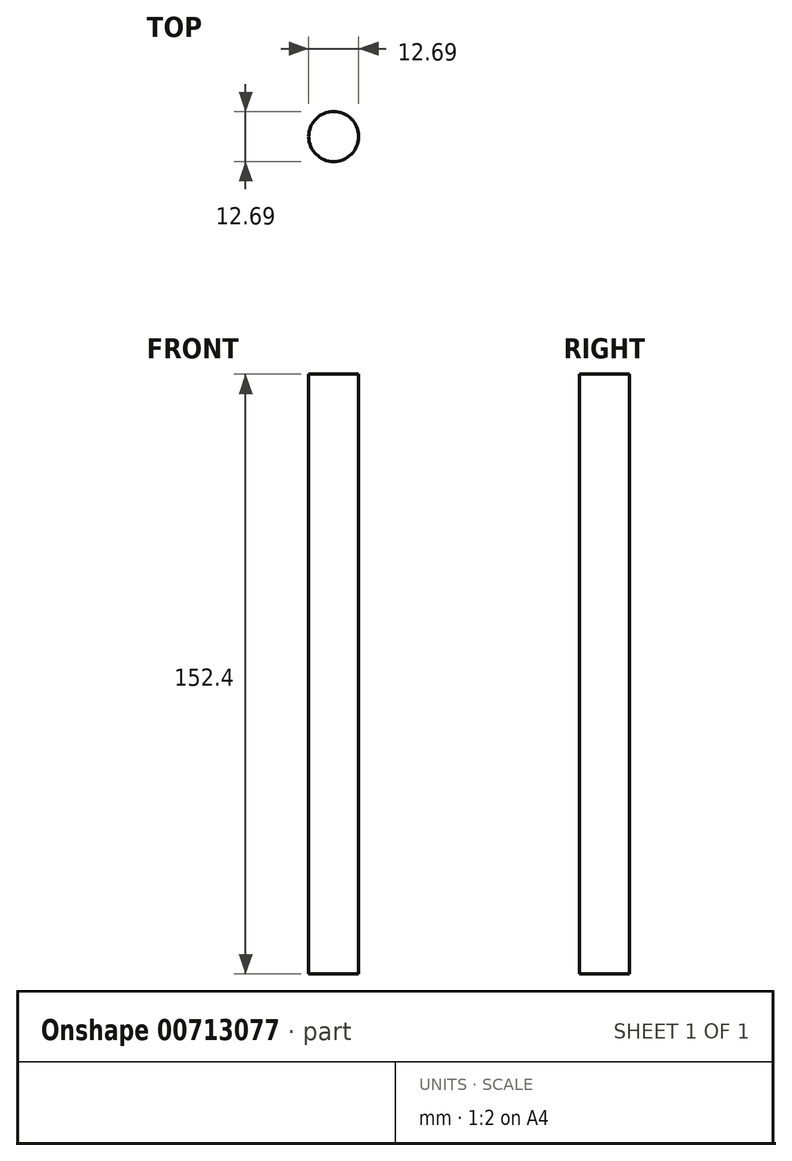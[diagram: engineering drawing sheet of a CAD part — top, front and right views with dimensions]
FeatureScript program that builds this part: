
annotation { "Feature Type Name" : "Feature", "Feature Type Description" : "" }
export const myFeature = defineFeature(function(context is Context, id is Id, definition is map)
    precondition{}
    {
        {
            var Q0;
            Q0=qCreatedBy(makeId("Top.planeOp"),FACE);
            var sketch = newSketch(context, id + "F0", { "sketchPlane" : qUnion([Q0])});
            skCircle(sketch, "E0", {"center": v(208.06, 3.86) * mm, "radius": 6.34 * mm});
            skSolve(sketch);
        }
        {
            var Q0;
            Q0=makeQuery(id+"F0.imprint","IMPRINT",FACE,{"disambiguationData":[TD([[makeQuery(id+"F0.imprint","IMPRINT",EDGE,{"derivedFrom":sQuery(id+"F0.wireOp",EDGE,"E0")}),1.0]])]});
            extrude(context, id + "F1", {"entities" : qUnion([Q0]), "depth" : 152.4 * mm});
        }
    });
